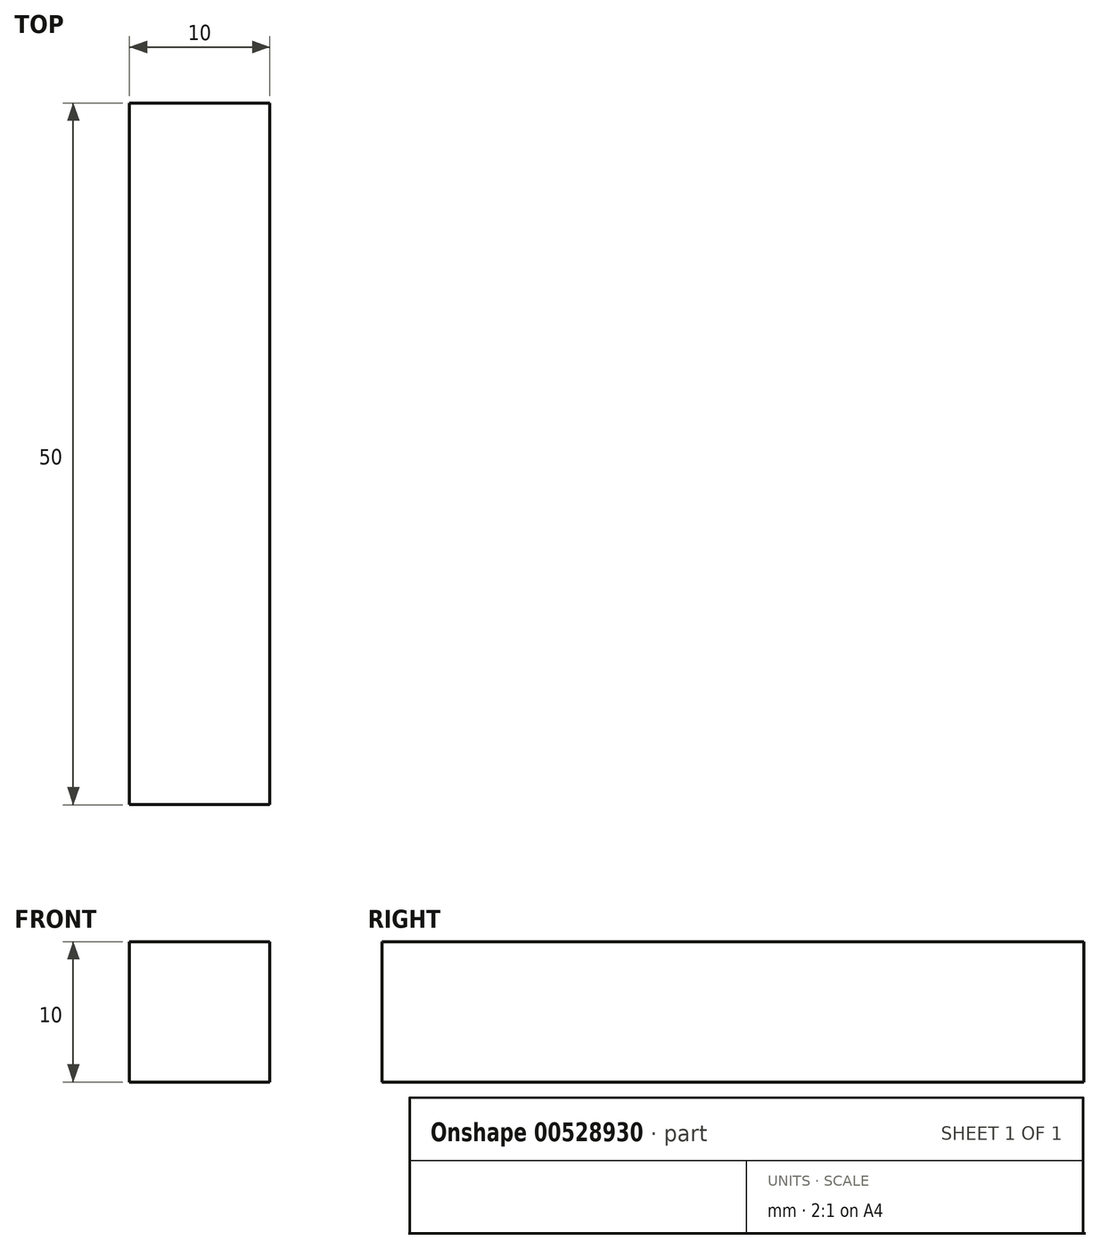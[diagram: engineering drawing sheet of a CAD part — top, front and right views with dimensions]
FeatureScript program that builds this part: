
annotation { "Feature Type Name" : "Feature", "Feature Type Description" : "" }
export const myFeature = defineFeature(function(context is Context, id is Id, definition is map)
    precondition{}
    {
        {
            var Q0;
            Q0=qCreatedBy(makeId("Top.planeOp"),FACE);
            var sketch = newSketch(context, id + "F0", { "sketchPlane" : qUnion([Q0])});
            skLineSegment(sketch, "E0.bottom", {"start": v(-54.46, 36.54) * mm, "end": v(-64.46, 36.54) * mm});
            skLineSegment(sketch, "E0.top", {"start": v(-54.46, 86.54) * mm, "end": v(-64.46, 86.54) * mm});
            skLineSegment(sketch, "E0.left", {"start": v(-54.46, 36.54) * mm, "end": v(-54.46, 86.54) * mm});
            skLineSegment(sketch, "E0.right", {"start": v(-64.46, 36.54) * mm, "end": v(-64.46, 86.54) * mm});
            skPoint(sketch, "E0.middle", {"position": v(-59.46, 61.54) * mm});
            skSolve(sketch);
        }
        {
            var Q0;
            Q0 = qSketchRegion(id + "F0", true);
            extrude(context, id + "F1", {"entities" : qUnion([Q0]), "depth" : 10 * mm, "offsetDistance" : 25 * mm});
        }
    });
